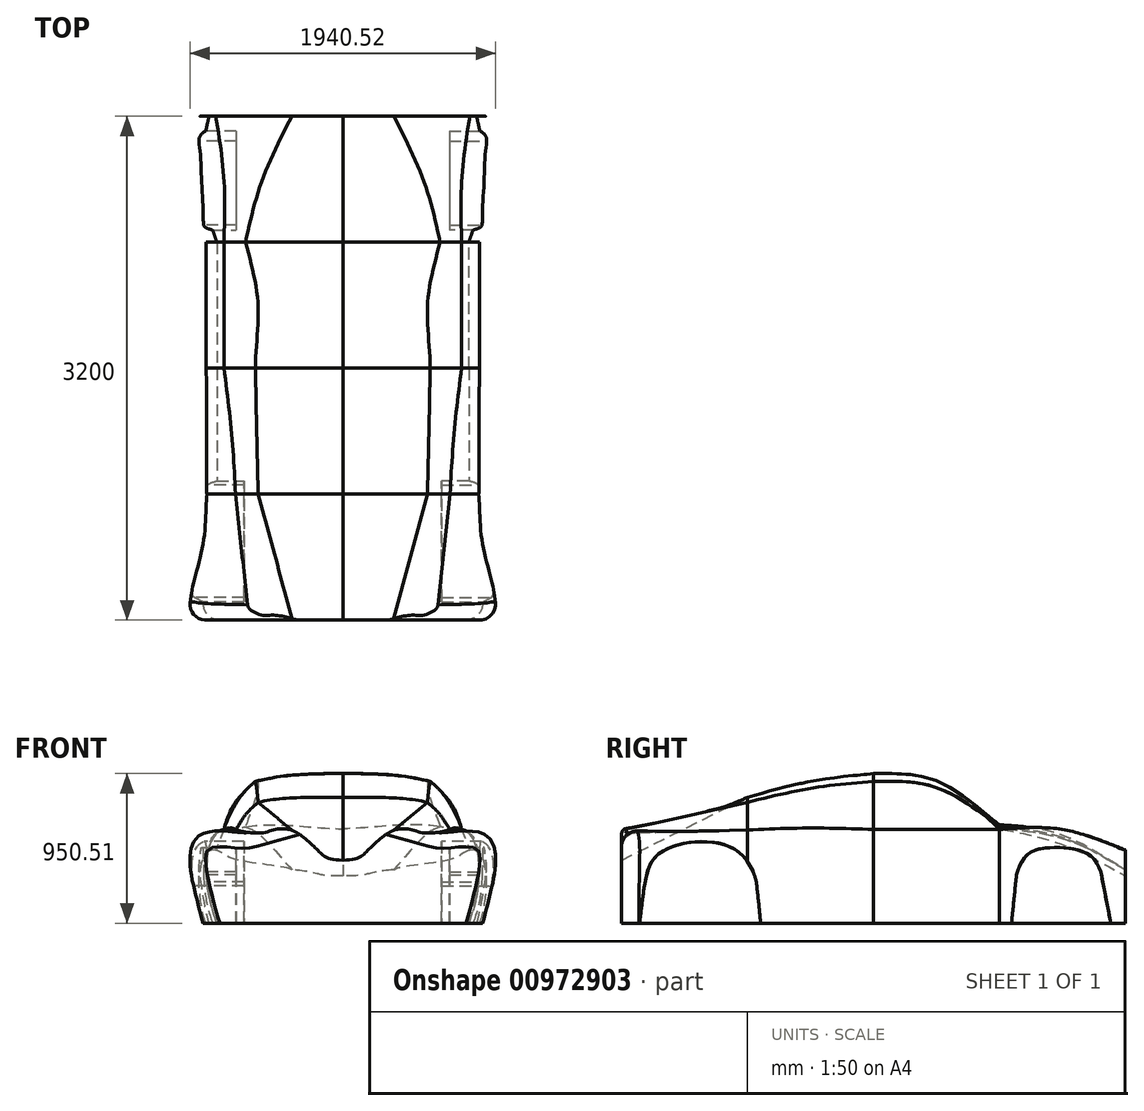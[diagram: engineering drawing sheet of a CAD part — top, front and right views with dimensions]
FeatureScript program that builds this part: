
annotation { "Feature Type Name" : "Feature", "Feature Type Description" : "" }
export const myFeature = defineFeature(function(context is Context, id is Id, definition is map)
    precondition{}
    {
        {
            var Q0;
            Q0=qCreatedBy(makeId("Front.planeOp"),FACE);
            cPlane(context, id + "F0", {"entities" : qUnion([Q0]), "cplaneType" : CPlaneType.OFFSET, "offset" : 400 * mm, "width" : 150 * mm, "height" : 150 * mm});
        }
        {
            var Q0;
            Q0=qCreatedBy(makeId("Front.planeOp"),FACE);
            cPlane(context, id + "F1", {"entities" : qUnion([Q0]), "cplaneType" : CPlaneType.OFFSET, "offset" : 400 * mm, "oppositeDirection" : true, "width" : 150 * mm, "height" : 150 * mm});
        }
        {
            var Q0;
            Q0=qCreatedBy(makeId("Front.planeOp"),FACE);
            cPlane(context, id + "F2", {"entities" : qUnion([Q0]), "cplaneType" : CPlaneType.OFFSET, "offset" : 800 * mm, "width" : 150 * mm, "height" : 150 * mm});
        }
        {
            var Q0;
            Q0=qCreatedBy(makeId("Front.planeOp"),FACE);
            cPlane(context, id + "F3", {"entities" : qUnion([Q0]), "cplaneType" : CPlaneType.OFFSET, "offset" : 800 * mm, "oppositeDirection" : true, "width" : 150 * mm, "height" : 150 * mm});
        }
        {
            var Q0;
            Q0=qCreatedBy(id+"F0.planeOp",FACE);
            var sketch = newSketch(context, id + "F4", { "sketchPlane" : qUnion([Q0])});
            skLineSegment(sketch, "E0", {"start": v(-437.64, -496.9) * mm, "end": v(362.36, -496.9) * mm});
            skFitSpline(sketch, "E1", {"points": [v(362.36, -496.9) * mm, v(411.37, -327.13) * mm, v(422.88, -64.41) * mm, v(362.36, 76.76) * mm, v(270.06, 107.64) * mm], "startDerivative": vector(197.67, 576.3) * mm, "endDerivative": vector(-315.03, 85.02) * mm});
            skFitSpline(sketch, "E2", {"points": [v(270.06, 107.64) * mm, v(225.54, 239.87) * mm, v(109.57, 359.67) * mm], "startDerivative": vector(-109.37, 364.31) * mm, "endDerivative": vector(-342.1, 275.59) * mm});
            skFitSpline(sketch, "E3", {"points": [v(109.57, 359.67) * mm, v(-93.9, 390.36) * mm, v(-437.64, 403.1) * mm], "startDerivative": vector(-435.27, 96.35) * mm, "endDerivative": vector(-663.86, -5.68) * mm});
            skLineSegment(sketch, "E4", {"start": v(-437.64, 403.1) * mm, "end": v(-437.64, -496.9) * mm});
            skSolve(sketch);
        }
        {
            var Q0;
            Q0=qCreatedBy(id+"F1.planeOp",FACE);
            var sketch = newSketch(context, id + "F5", { "sketchPlane" : qUnion([Q0])});
            skLineSegment(sketch, "E5", {"start": v(-437.64, -496.9) * mm, "end": v(362.36, -496.9) * mm});
            skFitSpline(sketch, "E6", {"points": [v(362.36, -496.9) * mm, v(411.37, -327.13) * mm, v(422.88, -64.41) * mm, v(362.36, 76.76) * mm, v(317.34, 98.7) * mm], "startDerivative": vector(197.67, 576.3) * mm, "endDerivative": vector(-315.03, 85.02) * mm});
            skFitSpline(sketch, "E7", {"points": [v(317.34, 98.7) * mm, v(233.9, 275.42) * mm, v(100.5, 364.64) * mm], "startDerivative": vector(-109.37, 364.31) * mm, "endDerivative": vector(-280.97, 134.3) * mm});
            skFitSpline(sketch, "E8", {"points": [v(100.5, 364.64) * mm, v(-101.44, 403.66) * mm, v(-437.64, 403.1) * mm], "startDerivative": vector(-435.27, 96.35) * mm, "endDerivative": vector(-663.86, -5.68) * mm});
            skLineSegment(sketch, "E9", {"start": v(-437.64, 403.1) * mm, "end": v(-437.64, -496.9) * mm});
            skSolve(sketch);
        }
        {
            var Q0;
            Q0=qCreatedBy(id+"F2.planeOp",FACE);
            var sketch = newSketch(context, id + "F6", { "sketchPlane" : qUnion([Q0])});
            skLineSegment(sketch, "E10", {"start": v(-437.64, -496.9) * mm, "end": v(362.36, -496.9) * mm});
            skFitSpline(sketch, "E11", {"points": [v(362.36, -496.9) * mm, v(411.37, -327.13) * mm, v(422.88, -64.41) * mm, v(362.36, 76.76) * mm, v(243.3, 95.74) * mm], "startDerivative": vector(197.67, 576.3) * mm, "endDerivative": vector(-315.03, 85.02) * mm});
            skFitSpline(sketch, "E12", {"points": [v(243.3, 95.74) * mm, v(189.7, 179.8) * mm, v(99.56, 271.16) * mm], "startDerivative": vector(-183.13, 286.64) * mm, "endDerivative": vector(-358.02, 310.73) * mm});
            skFitSpline(sketch, "E13", {"points": [v(99.56, 271.16) * mm, v(-96.57, 297.96) * mm, v(-437.64, 303.1) * mm], "startDerivative": vector(-435.27, 96.35) * mm, "endDerivative": vector(-663.86, -5.68) * mm});
            skLineSegment(sketch, "E14", {"start": v(-437.64, 303.1) * mm, "end": v(-437.64, -496.9) * mm});
            skSolve(sketch);
        }
        {
            var Q0;
            Q0=qCreatedBy(id+"F3.planeOp",FACE);
            var sketch = newSketch(context, id + "F7", { "sketchPlane" : qUnion([Q0])});
            skLineSegment(sketch, "E15", {"start": v(-437.64, -496.9) * mm, "end": v(362.36, -496.9) * mm});
            skFitSpline(sketch, "E16", {"points": [v(362.36, -496.9) * mm, v(411.37, -327.13) * mm, v(422.88, -64.41) * mm, v(362.36, 76.76) * mm, v(317.34, 98.7) * mm], "startDerivative": vector(197.67, 576.3) * mm, "endDerivative": vector(-315.03, 85.02) * mm});
            skFitSpline(sketch, "E17", {"points": [v(317.34, 98.7) * mm, v(232.34, 105.48) * mm, v(181.18, 115.23) * mm], "startDerivative": vector(-270.17, 31.04) * mm, "endDerivative": vector(-172.21, 37.01) * mm});
            skFitSpline(sketch, "E18", {"points": [v(181.18, 115.23) * mm, v(-108.75, 123.76) * mm, v(-437.64, 103.1) * mm], "startDerivative": vector(-435.27, 96.35) * mm, "endDerivative": vector(-663.86, -5.68) * mm});
            skLineSegment(sketch, "E19", {"start": v(-437.64, 103.1) * mm, "end": v(-437.64, -496.9) * mm});
            skSolve(sketch);
        }
        {
            var Q0;
            Q0=qCreatedBy(makeId("Front.planeOp"),FACE);
            var sketch = newSketch(context, id + "F8", { "sketchPlane" : qUnion([Q0])});
            skLineSegment(sketch, "E20", {"start": v(-437.64, -496.9) * mm, "end": v(362.36, -496.9) * mm});
            skFitSpline(sketch, "E21", {"points": [v(362.36, -496.9) * mm, v(411.37, -327.13) * mm, v(422.88, -64.41) * mm, v(362.36, 76.76) * mm, v(317.34, 98.7) * mm], "startDerivative": vector(197.67, 576.3) * mm, "endDerivative": vector(-315.03, 85.02) * mm});
            skFitSpline(sketch, "E22", {"points": [v(317.34, 98.7) * mm, v(233.9, 275.42) * mm, v(116.98, 404.65) * mm], "startDerivative": vector(-109.37, 364.31) * mm, "endDerivative": vector(-342.1, 275.59) * mm});
            skFitSpline(sketch, "E23", {"points": [v(116.98, 404.65) * mm, v(-86.1, 440.04) * mm, v(-437.64, 453.1) * mm], "startDerivative": vector(-435.27, 96.35) * mm, "endDerivative": vector(-663.86, -5.68) * mm});
            skLineSegment(sketch, "E24", {"start": v(-437.64, 453.1) * mm, "end": v(-437.64, -496.9) * mm});
            skSolve(sketch);
        }
        {
            var Q0;
            Q0=makeQuery(id+"F8.imprint","IMPRINT",FACE,{"disambiguationData":[TD([[makeQuery(id+"F8.imprint","IMPRINT",EDGE,{"derivedFrom":sQuery(id+"F8.wireOp",EDGE,"E20")}),1.0]])]});
            var Q1;
            Q1=makeQuery(id+"F4.imprint","IMPRINT",FACE,{"disambiguationData":[TD([[makeQuery(id+"F4.imprint","IMPRINT",EDGE,{"derivedFrom":sQuery(id+"F4.wireOp",EDGE,"E0")}),1.0]])]});
            var Q2;
            Q2=makeQuery(id+"F6.imprint","IMPRINT",FACE,{"disambiguationData":[TD([[makeQuery(id+"F6.imprint","IMPRINT",EDGE,{"derivedFrom":sQuery(id+"F6.wireOp",EDGE,"E10")}),1.0]])]});
            loft(context, id + "F9", {"sheetProfilesArray" : [{ "sheetProfileEntities" : qUnion([Q0]) }, { "sheetProfileEntities" : qUnion([Q1]) }, { "sheetProfileEntities" : qUnion([Q2]) }]});
        }
        {
            var Q1;
            Q1=makeQuery(id+"F9.opLoft","CAP_FACE",FACE,{"disambiguationData":[OSD([makeQuery(id+"F8.imprint","IMPRINT",FACE,{"disambiguationData":[TD([[makeQuery(id+"F8.imprint","IMPRINT",EDGE,{"derivedFrom":sQuery(id+"F8.wireOp",EDGE,"E20")}),1.0]])]})])],"isStart":true});
            var Q2;
            Q2=makeQuery(id+"F5.imprint","IMPRINT",FACE,{"disambiguationData":[TD([[makeQuery(id+"F5.imprint","IMPRINT",EDGE,{"derivedFrom":sQuery(id+"F5.wireOp",EDGE,"E5")}),1.0]])]});
            var Q3;
            Q3=makeQuery(id+"F7.imprint","IMPRINT",FACE,{"disambiguationData":[TD([[makeQuery(id+"F7.imprint","IMPRINT",EDGE,{"derivedFrom":sQuery(id+"F7.wireOp",EDGE,"E15")}),1.0]])]});
            loft(context, id + "F10", {"operationType" : NewBodyOperationType.ADD, "startCondition" : LoftEndDerivativeType.NORMAL_TO_PROFILE, "startMagnitude" : 1, "sheetProfilesArray" : [{ "sheetProfileEntities" : qUnion([Q1]) }, { "sheetProfileEntities" : qUnion([Q2]) }, { "sheetProfileEntities" : qUnion([Q3]) }]});
        }
        {
            var Q0;
            Q0=qCreatedBy(makeId("Front.planeOp"),FACE);
            cPlane(context, id + "F11", {"entities" : qUnion([Q0]), "cplaneType" : CPlaneType.OFFSET, "offset" : 1600 * mm, "width" : 150 * mm, "height" : 150 * mm});
        }
        {
            var Q0;
            Q0=qCreatedBy(id+"F11.planeOp",FACE);
            var sketch = newSketch(context, id + "F12", { "sketchPlane" : qUnion([Q0])});
            skLineSegment(sketch, "E25", {"start": v(-437.64, -496.9) * mm, "end": v(462.36, -496.9) * mm});
            skFitSpline(sketch, "E26", {"points": [v(462.36, -496.9) * mm, v(503.13, -340.23) * mm, v(548.82, -104.84) * mm, v(462.36, 76.76) * mm, v(157.92, 77.16) * mm], "startDerivative": vector(197.67, 576.3) * mm, "endDerivative": vector(-315.03, 85.02) * mm});
            skFitSpline(sketch, "E27", {"points": [v(157.92, 77.16) * mm, v(29.83, 81.91) * mm, v(-117.36, 91.62) * mm], "startDerivative": vector(-631.39, -51.17) * mm, "endDerivative": vector(-287.8, -108.16) * mm});
            skFitSpline(sketch, "E28", {"points": [v(-117.36, 91.62) * mm, v(-268.74, -23.15) * mm, v(-437.64, -96.9) * mm], "startDerivative": vector(-333.07, -142) * mm, "endDerivative": vector(-663.86, -5.68) * mm});
            skLineSegment(sketch, "E29", {"start": v(-437.64, -96.9) * mm, "end": v(-437.64, -496.9) * mm});
            skSolve(sketch);
        }
        {
            var Q1;
            Q1=qSketchRegion(id+"F12",true);
            var Q2;
            Q2=qSketchRegion(id+"F6",true);
            loft(context, id + "F13", {"operationType" : NewBodyOperationType.ADD, "sheetProfilesArray" : [{ "sheetProfileEntities" : qUnion([Q1]) }, { "sheetProfileEntities" : qUnion([Q2]) }]});
        }
        {
            var Q0;
            Q0=qCreatedBy(makeId("Right.planeOp"),FACE);
            cPlane(context, id + "F14", {"entities" : qUnion([Q0]), "cplaneType" : CPlaneType.OFFSET, "offset" : 800 * mm, "width" : 150 * mm, "height" : 150 * mm});
        }
        {
            var Q0;
            Q0=qCreatedBy(id+"F14.planeOp",FACE);
            var sketch = newSketch(context, id + "F15", { "sketchPlane" : qUnion([Q0])});
            skLineSegment(sketch, "E30", {"start": v(-743.36, -235.3) * mm, "end": v(-696.56, -680.73) * mm});
            skLineSegment(sketch, "E31", {"start": v(-696.56, -680.73) * mm, "end": v(-1508.45, -680.73) * mm});
            skLineSegment(sketch, "E32", {"start": v(-1508.45, -680.73) * mm, "end": v(-1455.6, -258.17) * mm});
            skFitSpline(sketch, "E33", {"points": [v(-1455.6, -258.17) * mm, v(-1367.73, -59.54) * mm, v(-939.89, 0) * mm, v(-743.36, -235.3) * mm], "startDerivative": vector(179.38, 766.9) * mm, "endDerivative": vector(215.74, -934.6) * mm});
            skSolve(sketch);
        }
        {
            var Q0;
            Q0=makeQuery(id+"F15.imprint","IMPRINT",FACE,{"disambiguationData":[TD([[makeQuery(id+"F15.imprint","IMPRINT",EDGE,{"derivedFrom":sQuery(id+"F15.wireOp",EDGE,"E30")}),-1.0]])]});
            extrude(context, id + "F16", {"entities" : qUnion([Q0]), "operationType" : NewBodyOperationType.REMOVE, "oppositeDirection" : true, "depth" : 610 * mm});
        }
        {
            var Q0;
            Q0=qCreatedBy(makeId("Front.planeOp"),FACE);
            cPlane(context, id + "F17", {"entities" : qUnion([Q0]), "cplaneType" : CPlaneType.OFFSET, "offset" : 1600 * mm, "oppositeDirection" : true, "width" : 150 * mm, "height" : 150 * mm});
        }
        {
            var Q0;
            Q0=qCreatedBy(id+"F17.planeOp",FACE);
            var sketch = newSketch(context, id + "F18", { "sketchPlane" : qUnion([Q0])});
            skLineSegment(sketch, "E34", {"start": v(-437.64, -496.9) * mm, "end": v(412.36, -496.9) * mm});
            skFitSpline(sketch, "E35", {"points": [v(412.36, -496.9) * mm, v(453.24, -312.76) * mm, v(468.47, -212.95) * mm, v(458.13, -104.07) * mm, v(368.95, -34.17) * mm], "startDerivative": vector(197.67, 576.3) * mm, "endDerivative": vector(-632.8, -161.78) * mm});
            skFitSpline(sketch, "E36", {"points": [v(368.95, -34.17) * mm, v(263.14, -86.74) * mm, v(-113.63, -157.63) * mm], "startDerivative": vector(-380.63, -87.62) * mm, "endDerivative": vector(-231.79, -133.75) * mm});
            skFitSpline(sketch, "E37", {"points": [v(-113.63, -157.63) * mm, v(-279.1, -183.63) * mm, v(-437.64, -196.9) * mm], "startDerivative": vector(-388.75, -15.86) * mm, "endDerivative": vector(-663.86, -5.68) * mm});
            skLineSegment(sketch, "E38", {"start": v(-437.64, -196.9) * mm, "end": v(-437.64, -496.9) * mm});
            skSolve(sketch);
        }
        {
            var Q0;
            Q0=qCreatedBy(id+"F17.planeOp",FACE);
            cPlane(context, id + "F19", {"entities" : qUnion([Q0]), "cplaneType" : CPlaneType.OFFSET, "offset" : 400 * mm, "width" : 150 * mm, "height" : 150 * mm});
        }
        {
            var Q0;
            Q0=qCreatedBy(id+"F19.planeOp",FACE);
            var sketch = newSketch(context, id + "F20", { "sketchPlane" : qUnion([Q0])});
            skLineSegment(sketch, "E39", {"start": v(-437.64, -496.9) * mm, "end": v(462.36, -496.9) * mm});
            skFitSpline(sketch, "E40", {"points": [v(462.36, -496.9) * mm, v(486.38, -325.83) * mm, v(475.5, -116.9) * mm, v(421.85, 53.8) * mm, v(317.34, 98.7) * mm], "startDerivative": vector(197.67, 576.3) * mm, "endDerivative": vector(-315.03, 85.02) * mm});
            skFitSpline(sketch, "E41", {"points": [v(317.34, 98.7) * mm, v(168.52, 51.04) * mm, v(72.04, 48.95) * mm], "startDerivative": vector(-360.94, 2.04) * mm, "endDerivative": vector(-390.07, 72.23) * mm});
            skFitSpline(sketch, "E42", {"points": [v(72.04, 48.95) * mm, v(-127.4, 56.45) * mm, v(-437.64, 3.1) * mm], "startDerivative": vector(-435.27, 96.35) * mm, "endDerivative": vector(-663.86, -5.68) * mm});
            skLineSegment(sketch, "E43", {"start": v(-437.64, 3.1) * mm, "end": v(-437.64, -496.9) * mm});
            skSolve(sketch);
        }
        {
            var Q1;
            Q1=makeQuery(id+"F10.opLoft","CAP_FACE",FACE,{"disambiguationData":[OSD([makeQuery(id+"F7.imprint","IMPRINT",FACE,{"disambiguationData":[TD([[makeQuery(id+"F7.imprint","IMPRINT",EDGE,{"derivedFrom":sQuery(id+"F7.wireOp",EDGE,"E15")}),1.0]])]})])],"isStart":true});
            var Q2;
            Q2=makeQuery(id+"F20.imprint","IMPRINT",FACE,{"disambiguationData":[TD([[makeQuery(id+"F20.imprint","IMPRINT",EDGE,{"derivedFrom":sQuery(id+"F20.wireOp",EDGE,"E39")}),1.0]])]});
            var Q3;
            Q3=makeQuery(id+"F18.imprint","IMPRINT",FACE,{"disambiguationData":[TD([[makeQuery(id+"F18.imprint","IMPRINT",EDGE,{"derivedFrom":sQuery(id+"F18.wireOp",EDGE,"E34")}),1.0]])]});
            loft(context, id + "F21", {"operationType" : NewBodyOperationType.ADD, "sheetProfilesArray" : [{ "sheetProfileEntities" : qUnion([Q1]) }, { "sheetProfileEntities" : qUnion([Q2]) }, { "sheetProfileEntities" : qUnion([Q3]) }]});
        }
        {
            var Q0;
            Q0=qCreatedBy(id+"F14.planeOp",FACE);
            var sketch = newSketch(context, id + "F22", { "sketchPlane" : qUnion([Q0])});
            skLineSegment(sketch, "E44", {"start": v(908.1, -190.95) * mm, "end": v(867.24, -590.52) * mm});
            skLineSegment(sketch, "E45", {"start": v(867.24, -590.52) * mm, "end": v(1525.62, -590.52) * mm});
            skLineSegment(sketch, "E46", {"start": v(1525.62, -590.52) * mm, "end": v(1443.9, -170.52) * mm});
            skFitSpline(sketch, "E47", {"points": [v(1443.9, -170.52) * mm, v(1357.62, -54.74) * mm, v(1166.92, -16.14) * mm, v(987.57, -54.74) * mm, v(908.1, -190.95) * mm], "startDerivative": vector(-221.05, 690.8) * mm, "endDerivative": vector(-187.84, -657.45) * mm});
            skSolve(sketch);
        }
        {
            var Q0;
            Q0=makeQuery(id+"F22.imprint","IMPRINT",FACE,{"disambiguationData":[TD([[makeQuery(id+"F22.imprint","IMPRINT",EDGE,{"derivedFrom":sQuery(id+"F22.wireOp",EDGE,"E44")}),1.0]])]});
            extrude(context, id + "F23", {"entities" : qUnion([Q0]), "operationType" : NewBodyOperationType.REMOVE, "oppositeDirection" : true, "depth" : 561 * mm});
        }
        {
            var Q0;
            {var subQ0=sQuery(id+"F8.wireOp",EDGE,"E24");var subQ1=sQuery(id+"F8.wireOp",EDGE,"E21");var subQ2=sQuery(id+"F8.wireOp",EDGE,"E20");Q0=makeQuery(id+"F21.boolean.opBoolean","MERGE",FACE,{"derivedFrom":[makeQuery(id+"F13.boolean.opBoolean","MERGE",FACE,{"derivedFrom":[makeQuery(id+"F10.boolean.opBoolean","MERGE",FACE,{"derivedFrom":[makeQuery(id+"F9.opLoft","SWEPT_FACE",FACE,{"disambiguationData":[OSD([sQuery(id+"F4.wireOp",EDGE,"E0"),sQuery(id+"F4.wireOp",EDGE,"E1"),sQuery(id+"F4.wireOp",EDGE,"E4"),subQ2,subQ1,subQ0])]}),makeQuery(id+"F10.opLoft","SWEPT_FACE",FACE,{"disambiguationData":[OSD([sQuery(id+"F5.wireOp",EDGE,"E5"),sQuery(id+"F5.wireOp",EDGE,"E6"),sQuery(id+"F5.wireOp",EDGE,"E9"),subQ2,subQ1,subQ0])]})]}),makeQuery(id+"F13.opLoft","SWEPT_FACE",FACE,{"disambiguationData":[OSD([sQuery(id+"F6.wireOp",EDGE,"E10"),sQuery(id+"F6.wireOp",EDGE,"E11"),sQuery(id+"F6.wireOp",EDGE,"E14"),sQuery(id+"F12.wireOp",EDGE,"E25"),sQuery(id+"F12.wireOp",EDGE,"E26"),sQuery(id+"F12.wireOp",EDGE,"E29")])]})]}),makeQuery(id+"F21.opLoft","SWEPT_FACE",FACE,{"disambiguationData":[OSD([sQuery(id+"F7.wireOp",EDGE,"E15"),sQuery(id+"F7.wireOp",EDGE,"E16"),sQuery(id+"F7.wireOp",EDGE,"E19"),sQuery(id+"F20.wireOp",EDGE,"E39"),sQuery(id+"F20.wireOp",EDGE,"E40"),sQuery(id+"F20.wireOp",EDGE,"E43")])]})]});}
            var sketch = newSketch(context, id + "F24", { "sketchPlane" : qUnion([Q0])});
            skFitSpline(sketch, "E48", {"points": [v(412.36, -1600) * mm, v(366.73, -1888.42) * mm, v(211.75, -2042.28) * mm, v(-139.29, -2091.57) * mm, v(-438.85, -2086.37) * mm], "startDerivative": vector(-69.7, -1240.37) * mm, "endDerivative": vector(-1120.26, 39.16) * mm});
            skLineSegment(sketch, "E49", {"start": v(-438.85, -2086.37) * mm, "end": v(-437.64, -1600) * mm});
            skLineSegment(sketch, "E50", {"start": v(-437.64, -1600) * mm, "end": v(412.36, -1600) * mm});
            skSolve(sketch);
        }
        {
            var Q0;
            Q0=makeQuery(id+"F13.opLoft","MID_CAP_EDGE",EDGE,{"disambiguationData":[OSD([sQuery(id+"F12.wireOp",EDGE,"E25"),sQuery(id+"F12.wireOp",EDGE,"E26"),sQuery(id+"F12.wireOp",EDGE,"E27")])],"capPos":0.0});
            fillet(context, id + "F25", {"entities" : qUnion([Q0]), "radius" : 100 * mm, "tangentPropagation" : true, "allowEdgeOverflow" : false});
        }
        {
            var Q0;
            Q0=makeQuery(id+"F9.opLoft","SWEPT_BODY",BODY,{"disambiguationData":[OSD([sQuery(id+"F4.wireOp",EDGE,"E2"),makeQuery(id+"F6.imprint","IMPRINT",FACE,{"disambiguationData":[TD([[makeQuery(id+"F6.imprint","IMPRINT",EDGE,{"derivedFrom":sQuery(id+"F6.wireOp",EDGE,"E10")}),1.0]])]}),makeQuery(id+"F8.imprint","IMPRINT",FACE,{"disambiguationData":[TD([[makeQuery(id+"F8.imprint","IMPRINT",EDGE,{"derivedFrom":sQuery(id+"F8.wireOp",EDGE,"E20")}),1.0]])]})])]});
            var Q1;
            {var subQ0=sQuery(id+"F8.wireOp",EDGE,"E24");var subQ1=sQuery(id+"F8.wireOp",EDGE,"E23");var subQ2=sQuery(id+"F8.wireOp",EDGE,"E20");Q1=makeQuery(id+"F21.boolean.opBoolean","MERGE",FACE,{"derivedFrom":[makeQuery(id+"F13.boolean.opBoolean","MERGE",FACE,{"derivedFrom":[makeQuery(id+"F10.boolean.opBoolean","MERGE",FACE,{"derivedFrom":[makeQuery(id+"F9.opLoft","SWEPT_FACE",FACE,{"disambiguationData":[OSD([sQuery(id+"F4.wireOp",EDGE,"E0"),sQuery(id+"F4.wireOp",EDGE,"E3"),sQuery(id+"F4.wireOp",EDGE,"E4"),subQ2,subQ1,subQ0])]}),makeQuery(id+"F10.opLoft","SWEPT_FACE",FACE,{"disambiguationData":[OSD([sQuery(id+"F5.wireOp",EDGE,"E5"),sQuery(id+"F5.wireOp",EDGE,"E8"),sQuery(id+"F5.wireOp",EDGE,"E9"),subQ2,subQ1,subQ0])]})]}),makeQuery(id+"F13.opLoft","SWEPT_FACE",FACE,{"disambiguationData":[OSD([sQuery(id+"F6.wireOp",EDGE,"E10"),sQuery(id+"F6.wireOp",EDGE,"E13"),sQuery(id+"F6.wireOp",EDGE,"E14"),sQuery(id+"F12.wireOp",EDGE,"E25"),sQuery(id+"F12.wireOp",EDGE,"E28"),sQuery(id+"F12.wireOp",EDGE,"E29")])]})]}),makeQuery(id+"F21.opLoft","SWEPT_FACE",FACE,{"disambiguationData":[OSD([sQuery(id+"F7.wireOp",EDGE,"E15"),sQuery(id+"F7.wireOp",EDGE,"E18"),sQuery(id+"F7.wireOp",EDGE,"E19"),sQuery(id+"F20.wireOp",EDGE,"E39"),sQuery(id+"F20.wireOp",EDGE,"E42"),sQuery(id+"F20.wireOp",EDGE,"E43")])]})]});}
            mirror(context, id + "F26", {"operationType" : NewBodyOperationType.ADD, "entities" : qUnion([Q0]), "mirrorPlane" : qUnion([Q1])});
        }
    });
